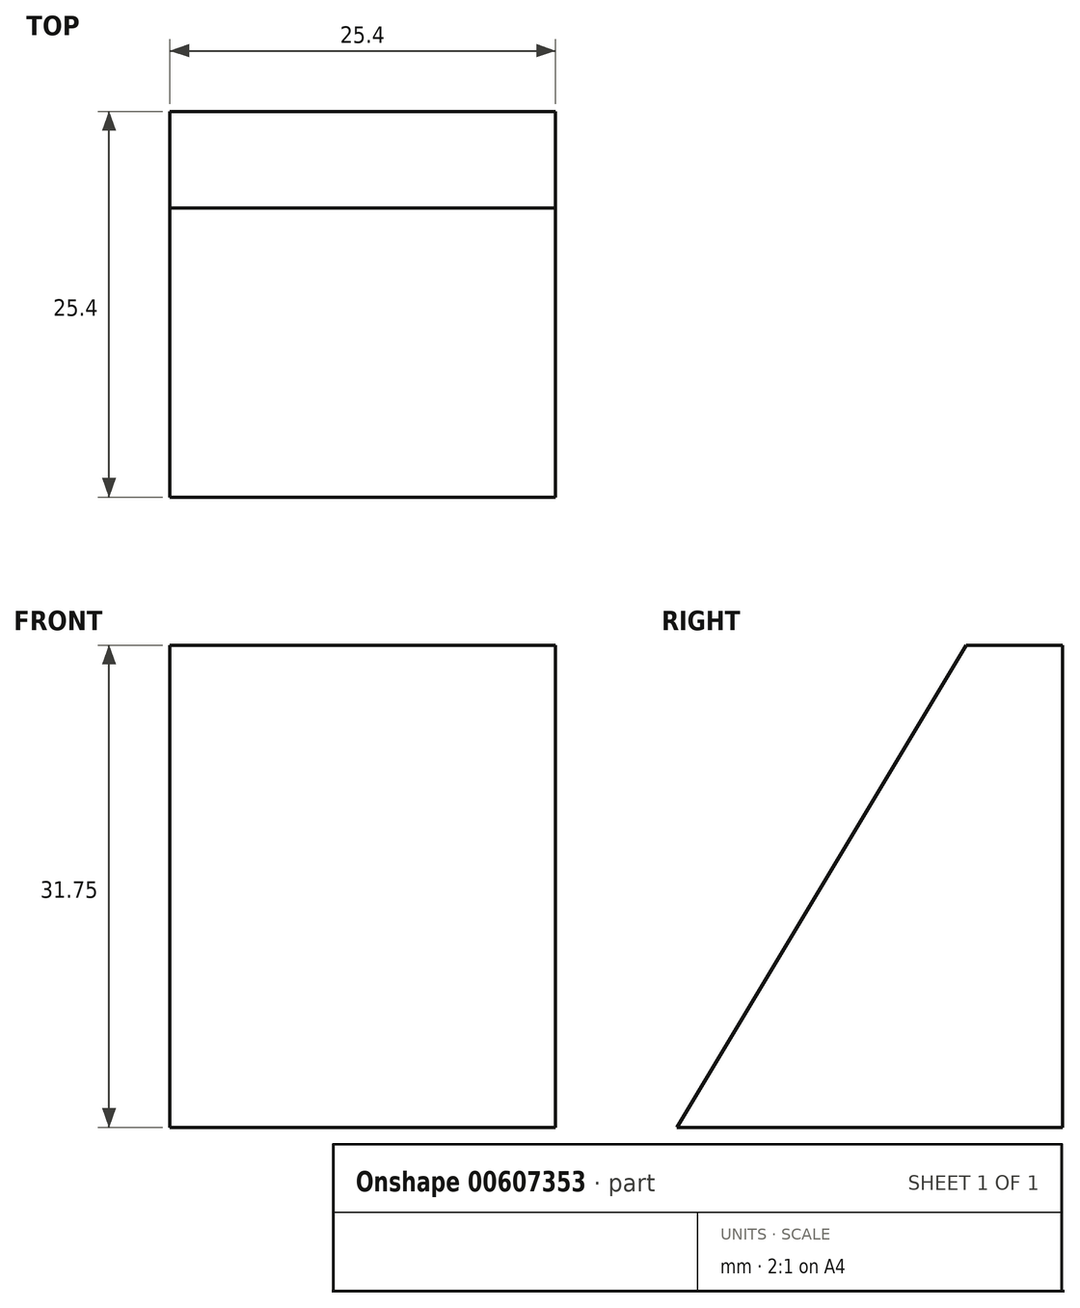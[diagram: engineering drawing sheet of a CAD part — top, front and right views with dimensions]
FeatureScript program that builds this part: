
annotation { "Feature Type Name" : "Feature", "Feature Type Description" : "" }
export const myFeature = defineFeature(function(context is Context, id is Id, definition is map)
    precondition{}
    {
        {
            var Q0;
            Q0=qCreatedBy(makeId("Top.planeOp"),FACE);
            var sketch = newSketch(context, id + "F0", { "sketchPlane" : qUnion([Q0])});
            skLineSegment(sketch, "E0", {"start": v(0, 0) * mm, "end": v(0, 38.1) * mm});
            skLineSegment(sketch, "E1", {"start": v(0, 38.1) * mm, "end": v(-25.4, 38.1) * mm});
            skLineSegment(sketch, "E2", {"start": v(-25.4, 38.1) * mm, "end": v(-25.4, 25.4) * mm});
            skLineSegment(sketch, "E3", {"start": v(-25.4, 25.4) * mm, "end": v(-6.35, 25.4) * mm});
            skLineSegment(sketch, "E4", {"start": v(-6.35, 25.4) * mm, "end": v(-6.35, 0) * mm});
            skLineSegment(sketch, "E5", {"start": v(-6.35, 0) * mm, "end": v(0, 0) * mm});
            skSolve(sketch);
        }
        {
            var Q0;
            Q0=makeQuery(id+"F0.imprint","IMPRINT",FACE,{"disambiguationData":[TD([[makeQuery(id+"F0.imprint","IMPRINT",EDGE,{"derivedFrom":sQuery(id+"F0.wireOp",EDGE,"E0")}),1.0]])]});
            extrude(context, id + "F1", {"entities" : qUnion([Q0]), "depth" : 31.75 * mm, "offsetDistance" : 25.4 * mm});
        }
        {
            var Q0;
            Q0=makeQuery(id+"F1.opExtrude","SWEPT_BODY",BODY,{"disambiguationData":[OSD([sQuery(id+"F0.wireOp",EDGE,"E0"),sQuery(id+"F0.wireOp",EDGE,"E1"),sQuery(id+"F0.wireOp",EDGE,"E2"),sQuery(id+"F0.wireOp",EDGE,"E3"),sQuery(id+"F0.wireOp",EDGE,"E4"),sQuery(id+"F0.wireOp",EDGE,"E5")])]});
            deleteBodies(context, id + "F2", {"entities" : qUnion([Q0])});
        }
        {
            var Q0;
            Q0=qCreatedBy(makeId("Right.planeOp"),FACE);
            var sketch = newSketch(context, id + "F3", { "sketchPlane" : qUnion([Q0])});
            skLineSegment(sketch, "E6", {"start": v(0, 0) * mm, "end": v(0, 31.75) * mm});
            skLineSegment(sketch, "E7", {"start": v(0, 0) * mm, "end": v(-25.4, 0) * mm});
            skLineSegment(sketch, "E8", {"start": v(-25.4, 0) * mm, "end": v(0, 0) * mm});
            skLineSegment(sketch, "E9", {"start": v(0, 31.75) * mm, "end": v(-6.35, 31.75) * mm});
            skLineSegment(sketch, "E10", {"start": v(-6.35, 31.75) * mm, "end": v(-25.4, 0) * mm});
            skSolve(sketch);
        }
        {
            var Q0;
            Q0=makeQuery(id+"F3.imprint","IMPRINT",FACE,{"disambiguationData":[TD([[makeQuery(id+"F3.imprint","IMPRINT",EDGE,{"derivedFrom":sQuery(id+"F3.wireOp",EDGE,"E6")}),1.0]])]});
            extrude(context, id + "F4", {"entities" : qUnion([Q0]), "depth" : 25.4 * mm, "offsetDistance" : 25.4 * mm});
        }
    });
